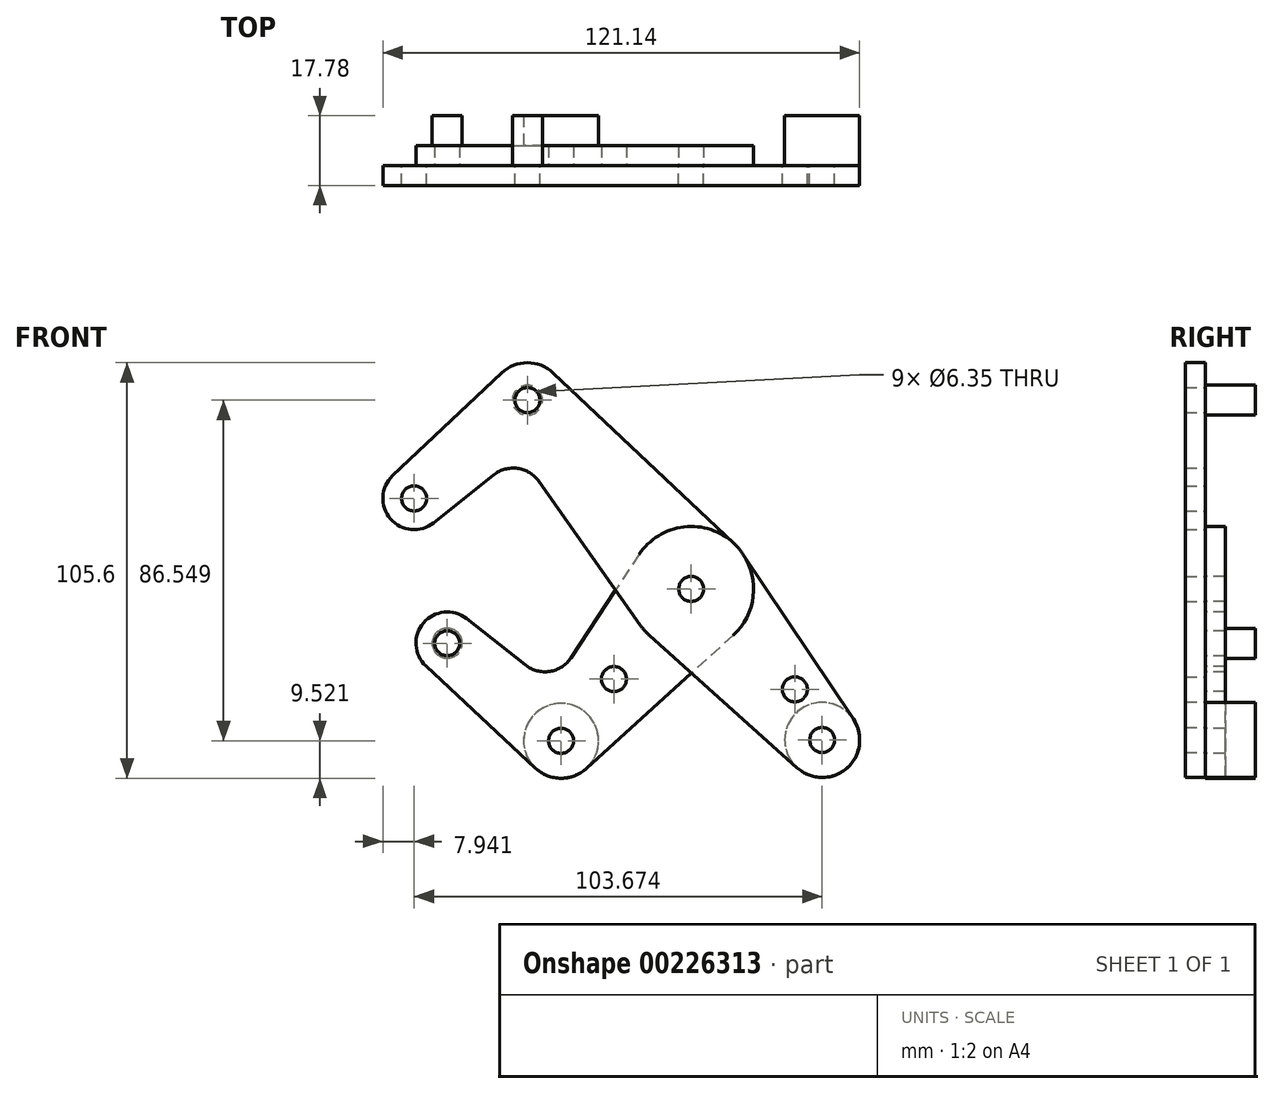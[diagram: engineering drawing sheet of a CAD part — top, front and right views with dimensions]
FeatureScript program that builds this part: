
annotation { "Feature Type Name" : "Feature", "Feature Type Description" : "" }
export const myFeature = defineFeature(function(context is Context, id is Id, definition is map)
    precondition{}
    {
        {
            var Q0;
            Q0=qCreatedBy(makeId("Front.planeOp"),FACE);
            var sketch = newSketch(context, id + "F0", { "sketchPlane" : qUnion([Q0])});
            skLineSegment(sketch, "E0", {"start": v(-41.6, 47.97) * mm, "end": v(41.6, -47.97) * mm, "construction": true});
            skCircle(sketch, "E1", {"center": v(0, 0) * mm, "radius": 3.18 * mm});
            skCircle(sketch, "E2", {"center": v(33.29, -38.38) * mm, "radius": 3.18 * mm});
            skCircle(sketch, "E3", {"center": v(-41.6, 47.97) * mm, "radius": 3.18 * mm});
            skCircle(sketch, "E4", {"center": v(-70.39, 23) * mm, "radius": 3.18 * mm});
            skLineSegment(sketch, "E5", {"start": v(-41.6, 47.97) * mm, "end": v(-70.39, 23) * mm, "construction": true});
            skCircle(sketch, "E6", {"center": v(33.29, -38.38) * mm, "radius": 9.53 * mm});
            skCircle(sketch, "E7", {"center": v(-70.39, 23) * mm, "radius": 7.94 * mm});
            skCircle(sketch, "E8", {"center": v(-41.6, 47.97) * mm, "radius": 9.53 * mm});
            skLineSegment(sketch, "E9", {"start": v(-75.83, 28.78) * mm, "end": v(-48.14, 54.9) * mm});
            skLineSegment(sketch, "E10", {"start": v(-65.44, 16.8) * mm, "end": v(-50.15, 28.98) * mm});
            skCircle(sketch, "E11", {"center": v(0, 0) * mm, "radius": 15.88 * mm});
            skLineSegment(sketch, "E12", {"start": v(-35.07, 54.9) * mm, "end": v(10.9, 11.55) * mm});
            skLineSegment(sketch, "E13", {"start": v(-38.72, 27.35) * mm, "end": v(-12.97, -9.15) * mm});
            skLineSegment(sketch, "E14", {"start": v(-10.6, -11.82) * mm, "end": v(26.93, -45.47) * mm});
            skLineSegment(sketch, "E15", {"start": v(13.2, 8.82) * mm, "end": v(41.2, -33.08) * mm});
            skArc(sketch, "E16.filletArc", {"start": v(-38.72, 27.35) * mm, "mid": v(-44.08, 30.63) * mm, "end": v(-50.15, 28.98) * mm});
            skLineSegment(sketch, "E17", {"start": v(0, 0) * mm, "end": v(-33.05, -38.58) * mm, "construction": true});
            skLineSegment(sketch, "E18", {"start": v(-33.05, -38.58) * mm, "end": v(-61.98, -13.8) * mm, "construction": true});
            skCircle(sketch, "E19", {"center": v(-61.98, -13.8) * mm, "radius": 3.18 * mm});
            skCircle(sketch, "E20", {"center": v(-33.05, -38.58) * mm, "radius": 3.18 * mm});
            skCircle(sketch, "E21", {"center": v(-61.98, -13.8) * mm, "radius": 7.94 * mm});
            skCircle(sketch, "E22", {"center": v(-33.05, -38.58) * mm, "radius": 9.53 * mm});
            skLineSegment(sketch, "E23", {"start": v(-57.08, -7.55) * mm, "end": v(-42.08, -19.35) * mm});
            skLineSegment(sketch, "E24", {"start": v(-67.4, -19.6) * mm, "end": v(-39.54, -45.55) * mm});
            skLineSegment(sketch, "E25", {"start": v(-13.25, 8.74) * mm, "end": v(-30.55, -17.48) * mm});
            skLineSegment(sketch, "E26", {"start": v(10.67, -11.75) * mm, "end": v(-26.65, -45.63) * mm});
            skArc(sketch, "E27.filletArc", {"start": v(-42.08, -19.35) * mm, "mid": v(-35.9, -20.95) * mm, "end": v(-30.55, -17.48) * mm});
            skCircle(sketch, "E28", {"center": v(-19.62, -22.9) * mm, "radius": 3.18 * mm});
            skCircle(sketch, "E29", {"center": v(26.32, -25.5) * mm, "radius": 3.18 * mm});
            skLineSegment(sketch, "E30", {"start": v(26.32, -25.5) * mm, "end": v(23.92, -27.58) * mm, "construction": true});
            skCircle(sketch, "E31", {"center": v(0, 0) * mm, "radius": 3.97 * mm});
            skSolve(sketch);
        }
        {
            var Q0;
            Q0=qCreatedBy(makeId("Front.planeOp"),FACE);
            cPlane(context, id + "F1", {"entities" : qUnion([Q0]), "cplaneType" : CPlaneType.OFFSET, "offset" : 12.7 * mm, "oppositeDirection" : true, "width" : 254 * mm, "height" : 254 * mm});
        }
        {
            var Q0;
            {var subQ1=sQuery(id+"F0.wireOp",EDGE,"E9");Q0=makeQuery(id+"F0.imprint","IMPRINT",FACE,{"disambiguationData":[TD([[makeQuery(id+"F0.imprint","IMPRINT",EDGE,{"derivedFrom":subQ1}),-1.0]])]});}
            var Q1;
            {var subQ0=sQuery(id+"F0.wireOp",EDGE,"E15");Q1=makeQuery(id+"F0.imprint","IMPRINT",FACE,{"disambiguationData":[TD([[makeQuery(id+"F0.imprint","IMPRINT",EDGE,{"derivedFrom":subQ0}),-1.0]])]});}
            var Q2;
            Q2=makeQuery(id+"F0.imprint","IMPRINT",FACE,{"disambiguationData":[TD([[makeQuery(id+"F0.imprint","IMPRINT",EDGE,{"derivedFrom":sQuery(id+"F0.wireOp",EDGE,"E2")}),-1.0]])]});
            var Q3;
            Q3=makeQuery(id+"F0.imprint","IMPRINT",FACE,{"disambiguationData":[TD([[makeQuery(id+"F0.imprint","IMPRINT",EDGE,{"derivedFrom":sQuery(id+"F0.wireOp",EDGE,"E4")}),-1.0]])]});
            var Q4;
            Q4=makeQuery(id+"F0.imprint","IMPRINT",FACE,{"disambiguationData":[TD([[makeQuery(id+"F0.imprint","IMPRINT",EDGE,{"derivedFrom":sQuery(id+"F0.wireOp",EDGE,"E3")}),-1.0]])]});
            var Q5;
            {var subQ0=sQuery(id+"F0.wireOp",EDGE,"E13");var subQ1=sQuery(id+"F0.wireOp",EDGE,"E11");var subQ2=makeQuery(id+"F0.imprint","INTERSECT",VERTEX,{"derivedFrom":[subQ1,subQ0]});Q5=makeQuery(id+"F0.imprint","IMPRINT",FACE,{"disambiguationData":[TD([[makeQuery(id+"F0.imprint","IMPRINT",EDGE,{"disambiguationData":[TD([[subQ2,1.0]])],"derivedFrom":subQ1}),-1.0]])]});}
            var Q6;
            {var subQ0=sQuery(id+"F0.wireOp",EDGE,"E14");var subQ1=sQuery(id+"F0.wireOp",EDGE,"E11");var subQ2=makeQuery(id+"F0.imprint","INTERSECT",VERTEX,{"derivedFrom":[subQ1,subQ0]});Q6=makeQuery(id+"F0.imprint","IMPRINT",FACE,{"disambiguationData":[TD([[makeQuery(id+"F0.imprint","IMPRINT",EDGE,{"disambiguationData":[TD([[subQ2,-1.0]])],"derivedFrom":subQ1}),-1.0]])]});}
            var Q7;
            Q7=makeQuery(id+"F0.imprint","IMPRINT",FACE,{"disambiguationData":[TD([[makeQuery(id+"F0.imprint","IMPRINT",EDGE,{"derivedFrom":sQuery(id+"F0.wireOp",EDGE,"E1")}),-1.0]])]});
            var Q8;
            Q8=makeQuery(id+"F0.imprint","IMPRINT",FACE,{"disambiguationData":[TD([[makeQuery(id+"F0.imprint","IMPRINT",EDGE,{"derivedFrom":sQuery(id+"F0.wireOp",EDGE,"E31")}),-1.0]])]});
            extrude(context, id + "F2", {"entities" : qUnion([Q0, Q1, Q2, Q3, Q4, Q5, Q6, Q7, Q8]), "depth" : 5.08 * mm});
        }
        {
            var Q0;
            {var subQ10=sQuery(id+"F0.wireOp",EDGE,"E23");Q0=makeQuery(id+"F0.imprint","IMPRINT",FACE,{"disambiguationData":[TD([[makeQuery(id+"F0.imprint","IMPRINT",EDGE,{"derivedFrom":subQ10}),-1.0]])]});}
            var Q1;
            Q1=makeQuery(id+"F0.imprint","IMPRINT",FACE,{"disambiguationData":[TD([[makeQuery(id+"F0.imprint","IMPRINT",EDGE,{"derivedFrom":sQuery(id+"F0.wireOp",EDGE,"E19")}),-1.0]])]});
            var Q2;
            Q2=makeQuery(id+"F0.imprint","IMPRINT",FACE,{"disambiguationData":[TD([[makeQuery(id+"F0.imprint","IMPRINT",EDGE,{"derivedFrom":sQuery(id+"F0.wireOp",EDGE,"E20")}),-1.0]])]});
            var Q3;
            Q3=makeQuery(id+"F0.imprint","IMPRINT",FACE,{"disambiguationData":[TD([[makeQuery(id+"F0.imprint","IMPRINT",EDGE,{"derivedFrom":sQuery(id+"F0.wireOp",EDGE,"E31")}),-1.0]])]});
            var Q4;
            {var subQ0=sQuery(id+"F0.wireOp",EDGE,"E14");var subQ1=sQuery(id+"F0.wireOp",EDGE,"E11");var subQ2=makeQuery(id+"F0.imprint","INTERSECT",VERTEX,{"derivedFrom":[subQ1,subQ0]});Q4=makeQuery(id+"F0.imprint","IMPRINT",FACE,{"disambiguationData":[TD([[makeQuery(id+"F0.imprint","IMPRINT",EDGE,{"disambiguationData":[TD([[subQ2,-1.0]])],"derivedFrom":subQ1}),-1.0]])]});}
            var Q5;
            {var subQ0=sQuery(id+"F0.wireOp",EDGE,"E13");var subQ1=sQuery(id+"F0.wireOp",EDGE,"E11");var subQ2=makeQuery(id+"F0.imprint","INTERSECT",VERTEX,{"derivedFrom":[subQ1,subQ0]});Q5=makeQuery(id+"F0.imprint","IMPRINT",FACE,{"disambiguationData":[TD([[makeQuery(id+"F0.imprint","IMPRINT",EDGE,{"disambiguationData":[TD([[subQ2,1.0]])],"derivedFrom":subQ1}),-1.0]])]});}
            var Q6;
            Q6=makeQuery(id+"F0.imprint","IMPRINT",FACE,{"disambiguationData":[TD([[makeQuery(id+"F0.imprint","IMPRINT",EDGE,{"derivedFrom":sQuery(id+"F0.wireOp",EDGE,"E1")}),-1.0]])]});
            extrude(context, id + "F3", {"entities" : qUnion([Q0, Q1, Q2, Q3, Q4, Q5, Q6]), "oppositeDirection" : true, "depth" : 5.08 * mm});
        }
        {
            var Q0;
            {var subQ0=sQuery(id+"F0.wireOp",EDGE,"E15");Q0=makeQuery(id+"F0.imprint","IMPRINT",FACE,{"disambiguationData":[TD([[makeQuery(id+"F0.imprint","IMPRINT",EDGE,{"derivedFrom":subQ0}),-1.0]])]});}
            var sketch = newSketch(context, id + "F4", { "sketchPlane" : qUnion([Q0])});
            skCircle(sketch, "E32.0", {"center": v(33.29, -38.38) * mm, "radius": 9.53 * mm});
            skPoint(sketch, "E33.0", {"position": v(-41.6, 47.97) * mm});
            skCircle(sketch, "E34", {"center": v(-41.6, 47.97) * mm, "radius": 3.81 * mm});
            skSolve(sketch);
        }
        {
            var Q0;
            Q0=makeQuery(id+"F3.opExtrude","CAP_FACE",FACE,{"disambiguationData":[OSD([sQuery(id+"F0.wireOp",EDGE,"E1"),sQuery(id+"F0.wireOp",EDGE,"E11"),sQuery(id+"F0.wireOp",EDGE,"E19"),sQuery(id+"F0.wireOp",EDGE,"E20"),sQuery(id+"F0.wireOp",EDGE,"E21"),sQuery(id+"F0.wireOp",EDGE,"E22"),sQuery(id+"F0.wireOp",EDGE,"E23"),sQuery(id+"F0.wireOp",EDGE,"E24"),sQuery(id+"F0.wireOp",EDGE,"E25"),sQuery(id+"F0.wireOp",EDGE,"E26"),sQuery(id+"F0.wireOp",EDGE,"E27.filletArc"),sQuery(id+"F0.wireOp",EDGE,"E28")])],"isStart":false});
            var sketch = newSketch(context, id + "F5", { "sketchPlane" : qUnion([Q0])});
            skCircle(sketch, "E35.0", {"center": v(33.05, -38.58) * mm, "radius": 9.53 * mm});
            skCircle(sketch, "E36", {"center": v(61.98, -13.8) * mm, "radius": 3.8 * mm});
            skSolve(sketch);
        }
        {
            var Q0;
            Q0 = qSketchRegion(id + "F4", true);
            var Q1;
            Q1 = qSketchRegion(id + "F5", true);
            var Q2;
            Q2=qCreatedBy(id+"F1.planeOp",FACE);
            extrude(context, id + "F6", {"entities" : qUnion([Q0, Q1]), "endBound" : BoundingType.UP_TO_SURFACE, "oppositeDirection" : true, "endBoundEntityFace" : qUnion([Q2]), "depth" : 25.4 * mm});
        }
    });
